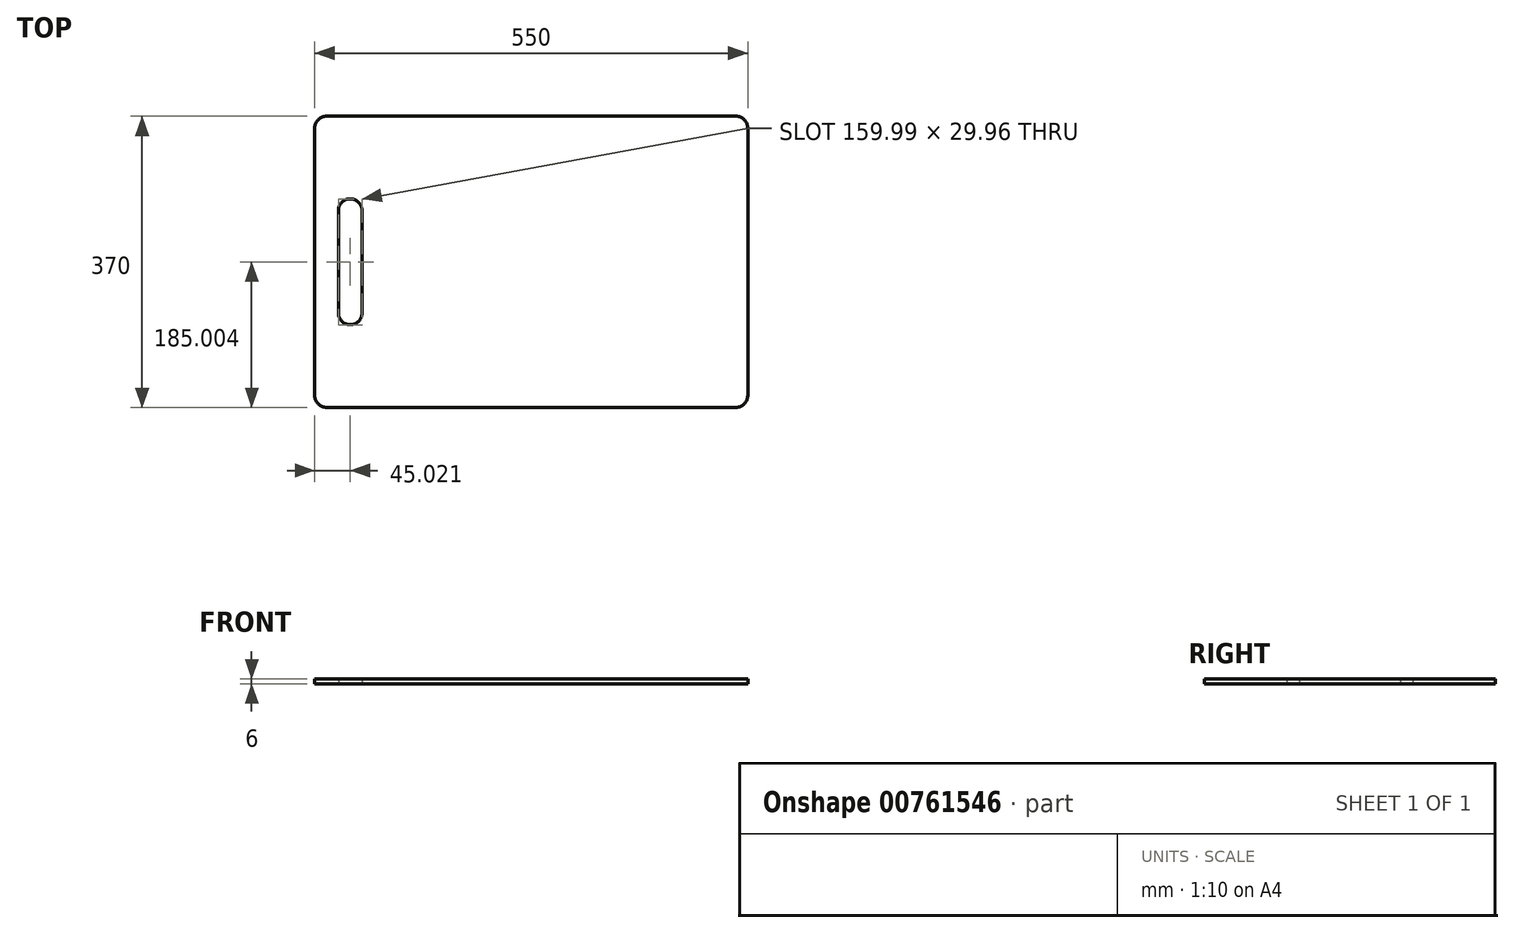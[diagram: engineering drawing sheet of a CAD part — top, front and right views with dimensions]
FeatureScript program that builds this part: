
annotation { "Feature Type Name" : "Feature", "Feature Type Description" : "" }
export const myFeature = defineFeature(function(context is Context, id is Id, definition is map)
    precondition{}
    {
        {
            var Q0;
            Q0=qCreatedBy(makeId("Top.planeOp"),FACE);
            var sketch = newSketch(context, id + "F0", { "sketchPlane" : qUnion([Q0])});
            skLineSegment(sketch, "E0.bottom", {"start": v(260, 185) * mm, "end": v(-260, 185) * mm});
            skLineSegment(sketch, "E0.top", {"start": v(260, -185) * mm, "end": v(-260, -185) * mm});
            skLineSegment(sketch, "E0.left", {"start": v(275, 170) * mm, "end": v(275, -170) * mm});
            skLineSegment(sketch, "E0.right", {"start": v(-275, 170) * mm, "end": v(-275, -170) * mm});
            skPoint(sketch, "E0.middle", {"position": v(0, 0) * mm});
            skPoint(sketch, "E1.visualSharp", {"position": v(-275, 185) * mm});
            skArc(sketch, "E1.filletArc", {"start": v(-260, 185) * mm, "mid": v(-270.6, 180.6) * mm, "end": v(-275, 170) * mm});
            skPoint(sketch, "E2.visualSharp", {"position": v(-275, -185) * mm});
            skArc(sketch, "E2.filletArc", {"start": v(-275, -170) * mm, "mid": v(-270.6, -180.6) * mm, "end": v(-260, -185) * mm});
            skPoint(sketch, "E3.visualSharp", {"position": v(275, 185) * mm});
            skArc(sketch, "E3.filletArc", {"start": v(275, 170) * mm, "mid": v(270.6, 180.6) * mm, "end": v(260, 185) * mm});
            skPoint(sketch, "E4.visualSharp", {"position": v(275, -185) * mm});
            skArc(sketch, "E4.filletArc", {"start": v(260, -185) * mm, "mid": v(270.6, -180.6) * mm, "end": v(275, -170) * mm});
            skArc(sketch, "E5", {"start": v(-215.02, 64.32) * mm, "mid": v(-230.22, 80) * mm, "end": v(-244.96, 63.9) * mm});
            skArc(sketch, "E6", {"start": v(-244.96, -63.9) * mm, "mid": v(-230.55, -79.99) * mm, "end": v(-215, -65) * mm});
            skLineSegment(sketch, "E7", {"start": v(-215.02, 65.68) * mm, "end": v(-215, -65) * mm});
            skLineSegment(sketch, "E8", {"start": v(-244.96, -66.1) * mm, "end": v(-244.96, 66.1) * mm});
            skSolve(sketch);
        }
        {
            var Q0;
            Q0 = qSketchRegion(id + "F0", true);
            extrude(context, id + "F1", {"entities" : qUnion([Q0]), "depth" : 6 * mm, "offsetDistance" : 25 * mm});
        }
    });
